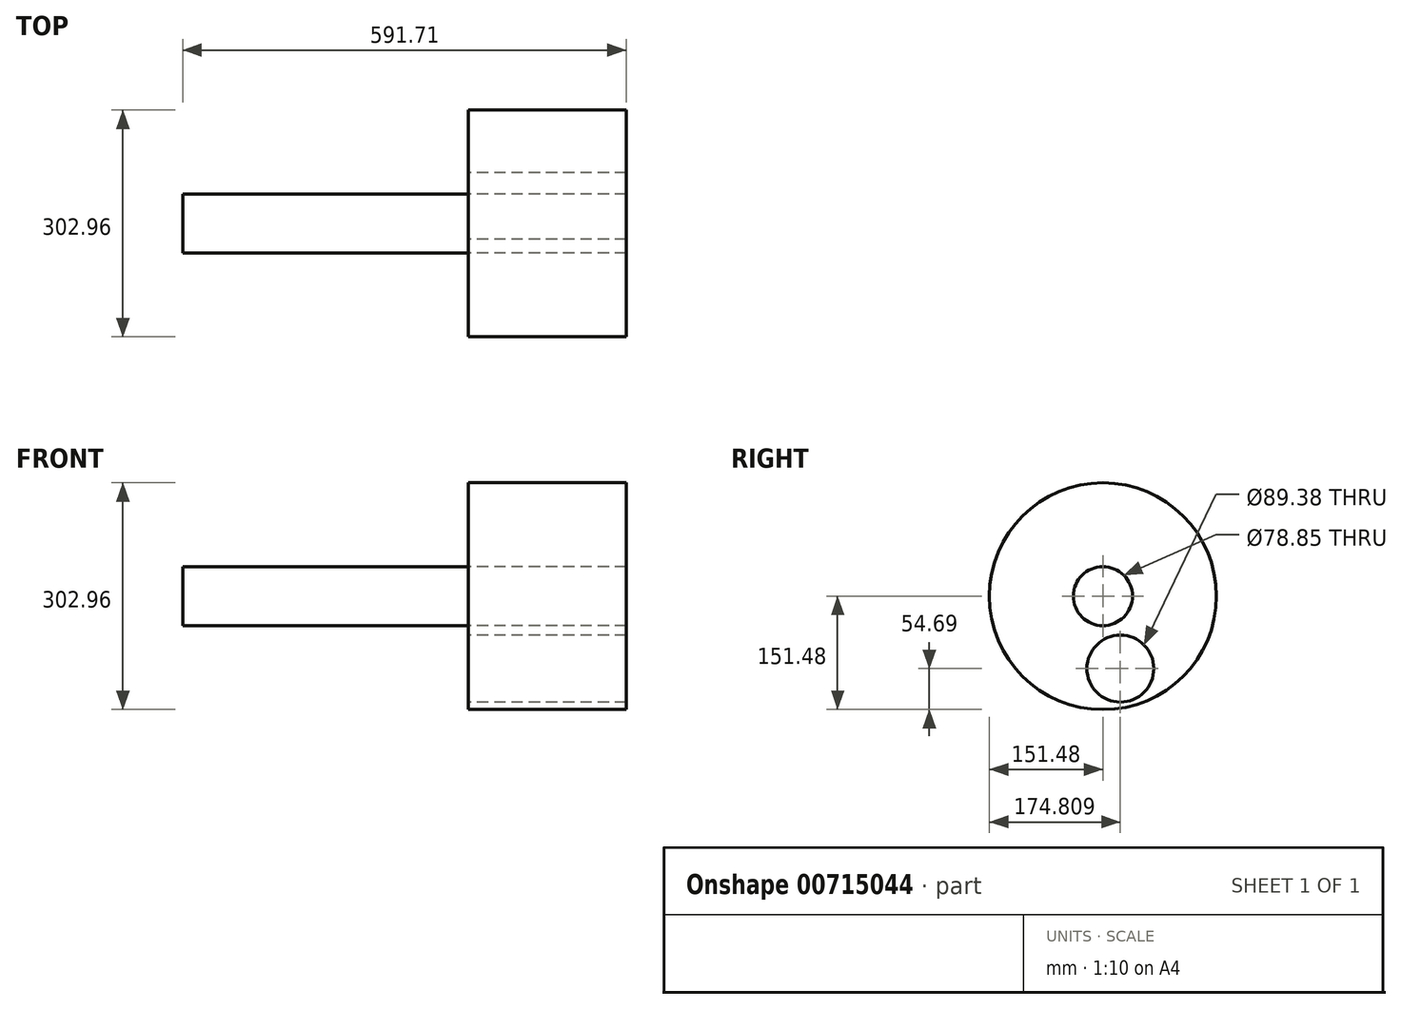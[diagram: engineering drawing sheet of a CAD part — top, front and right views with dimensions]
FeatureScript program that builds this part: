
annotation { "Feature Type Name" : "Feature", "Feature Type Description" : "" }
export const myFeature = defineFeature(function(context is Context, id is Id, definition is map)
    precondition{}
    {
        {
            var Q0;
            Q0=qCreatedBy(makeId("Right.planeOp"),FACE);
            var sketch = newSketch(context, id + "F0", { "sketchPlane" : qUnion([Q0])});
            skCircle(sketch, "E0", {"center": v(0, 0) * mm, "radius": 39.43 * mm});
            skSolve(sketch);
        }
        {
            var Q0;
            Q0 = qSketchRegion(id + "F0", true);
            var Q1;
            Q1=sQuery(id+"F0.wireOp",EDGE,"E0");
            extrude(context, id + "F1", {"entities" : qUnion([Q0]), "surfaceOperationType" : NewSurfaceOperationType.ADD, "surfaceEntities" : qUnion([Q1]), "depth" : 381 * mm, "offsetDistance" : 25.4 * mm});
        }
        {
            var Q0;
            Q0=makeQuery(id+"F1.opExtrude","CAP_FACE",FACE,{"disambiguationData":[OSD([sQuery(id+"F0.wireOp",EDGE,"E0")])],"isStart":false});
            var sketch = newSketch(context, id + "F2", { "sketchPlane" : qUnion([Q0])});
            skCircle(sketch, "E1", {"center": v(0, 0) * mm, "radius": 151.48 * mm});
            skCircle(sketch, "E2", {"center": v(23.33, -96.79) * mm, "radius": 44.69 * mm});
            skSolve(sketch);
        }
        {
            var Q0;
            Q0=makeQuery(id+"F2.imprint","IMPRINT",FACE,{"disambiguationData":[TD([[makeQuery(id+"F2.imprint","IMPRINT",EDGE,{"derivedFrom":sQuery(id+"F2.wireOp",EDGE,"E1")}),1.0]])]});
            extrude(context, id + "F3", {"entities" : qUnion([Q0]), "depth" : 210.71 * mm, "offsetDistance" : 25.4 * mm});
        }
    });
